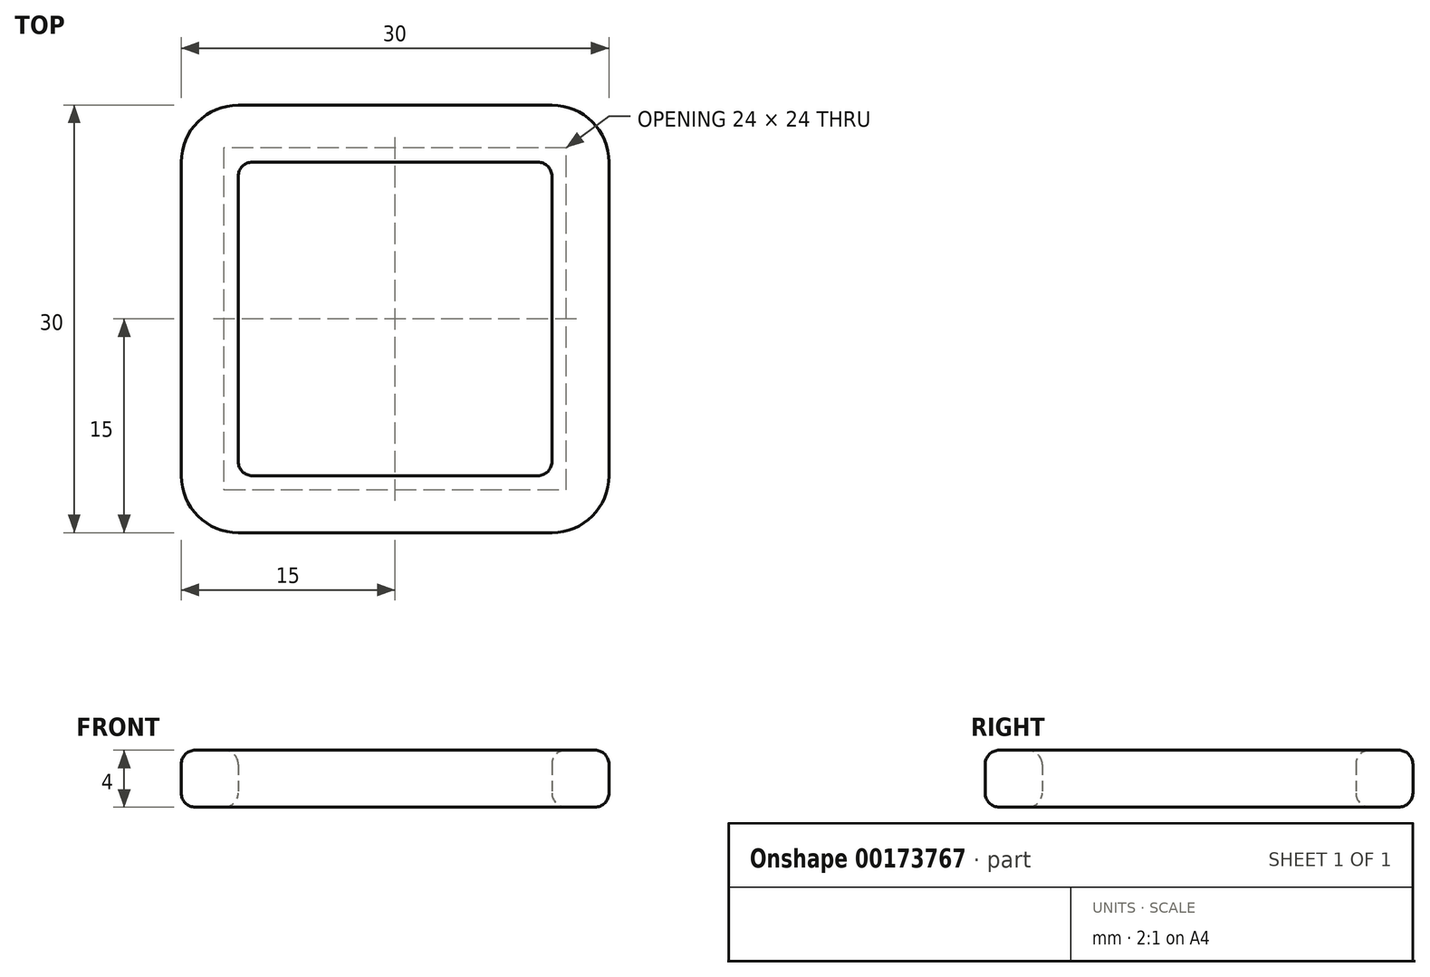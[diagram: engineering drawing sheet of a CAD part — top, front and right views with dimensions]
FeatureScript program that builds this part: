
annotation { "Feature Type Name" : "Feature", "Feature Type Description" : "" }
export const myFeature = defineFeature(function(context is Context, id is Id, definition is map)
    precondition{}
    {
        {
            var Q0;
            Q0=qCreatedBy(makeId("Top.planeOp"),FACE);
            var sketch = newSketch(context, id + "F0", { "sketchPlane" : qUnion([Q0])});
            skLineSegment(sketch, "E0.bottom", {"start": v(15, 15) * mm, "end": v(-15, 15) * mm});
            skLineSegment(sketch, "E0.top", {"start": v(15, -15) * mm, "end": v(-15, -15) * mm});
            skLineSegment(sketch, "E0.left", {"start": v(15, 15) * mm, "end": v(15, -15) * mm});
            skLineSegment(sketch, "E0.right", {"start": v(-15, 15) * mm, "end": v(-15, -15) * mm});
            skPoint(sketch, "E0.middle", {"position": v(0, 0) * mm});
            skSolve(sketch);
        }
        {
            var Q0;
            Q0=makeQuery(id+"F0.imprint","IMPRINT",FACE,{"disambiguationData":[TD([[makeQuery(id+"F0.imprint","IMPRINT",EDGE,{"derivedFrom":sQuery(id+"F0.wireOp",EDGE,"E0.bottom")}),1.0]])]});
            extrude(context, id + "F1", {"entities" : qUnion([Q0]), "depth" : 4 * mm});
        }
        {
            var Q0;
            Q0=makeQuery(id+"F1.opExtrude","CAP_FACE",FACE,{"disambiguationData":[OSD([sQuery(id+"F0.wireOp",EDGE,"E0.bottom"),sQuery(id+"F0.wireOp",EDGE,"E0.top"),sQuery(id+"F0.wireOp",EDGE,"E0.left"),sQuery(id+"F0.wireOp",EDGE,"E0.right")])],"isStart":false});
            var Q1;
            Q1=makeQuery(id+"F1.opExtrude","CAP_FACE",FACE,{"disambiguationData":[OSD([sQuery(id+"F0.wireOp",EDGE,"E0.bottom"),sQuery(id+"F0.wireOp",EDGE,"E0.top"),sQuery(id+"F0.wireOp",EDGE,"E0.left"),sQuery(id+"F0.wireOp",EDGE,"E0.right")])],"isStart":true});
            shell(context, id + "F2", {"entities" : qUnion([Q0, Q1]), "thickness" : 4 * mm});
        }
        {
            var Q0;
            Q0=makeQuery(id+"F2.opShell","OFFSET_EDGE",EDGE,{"disambiguationData":[OSD([sQuery(id+"F0.wireOp",EDGE,"E0.bottom"),sQuery(id+"F0.wireOp",EDGE,"E0.right")])]});
            var Q1;
            Q1=makeQuery(id+"F2.opShell","OFFSET_EDGE",EDGE,{"disambiguationData":[OSD([sQuery(id+"F0.wireOp",EDGE,"E0.bottom"),sQuery(id+"F0.wireOp",EDGE,"E0.left")])]});
            var Q2;
            Q2=makeQuery(id+"F2.opShell","OFFSET_EDGE",EDGE,{"disambiguationData":[OSD([sQuery(id+"F0.wireOp",EDGE,"E0.top"),sQuery(id+"F0.wireOp",EDGE,"E0.right")])]});
            var Q3;
            Q3=makeQuery(id+"F2.opShell","OFFSET_EDGE",EDGE,{"disambiguationData":[OSD([sQuery(id+"F0.wireOp",EDGE,"E0.top"),sQuery(id+"F0.wireOp",EDGE,"E0.left")])]});
            fillet(context, id + "F3", {"entities" : qUnion([Q0, Q1, Q2, Q3]), "radius" : 1 * mm, "tangentPropagation" : true, "allowEdgeOverflow" : false});
        }
        {
            var Q0;
            Q0=makeQuery(id+"F1.opExtrude","SWEPT_EDGE",EDGE,{"disambiguationData":[OSD([sQuery(id+"F0.wireOp",EDGE,"E0.bottom"),sQuery(id+"F0.wireOp",EDGE,"E0.right")])]});
            var Q1;
            Q1=makeQuery(id+"F1.opExtrude","SWEPT_EDGE",EDGE,{"disambiguationData":[OSD([sQuery(id+"F0.wireOp",EDGE,"E0.bottom"),sQuery(id+"F0.wireOp",EDGE,"E0.left")])]});
            var Q2;
            Q2=makeQuery(id+"F1.opExtrude","SWEPT_EDGE",EDGE,{"disambiguationData":[OSD([sQuery(id+"F0.wireOp",EDGE,"E0.top"),sQuery(id+"F0.wireOp",EDGE,"E0.right")])]});
            var Q3;
            Q3=makeQuery(id+"F1.opExtrude","SWEPT_EDGE",EDGE,{"disambiguationData":[OSD([sQuery(id+"F0.wireOp",EDGE,"E0.top"),sQuery(id+"F0.wireOp",EDGE,"E0.left")])]});
            fillet(context, id + "F4", {"entities" : qUnion([Q0, Q1, Q2, Q3]), "radius" : 4 * mm, "tangentPropagation" : true, "allowEdgeOverflow" : false});
        }
        {
            var Q0;
            {var subQ0=sQuery(id+"F0.wireOp",EDGE,"E0.left");Q0=makeQuery(id+"F2.opShell","OFFSET_EDGE",EDGE,{"disambiguationData":[OSD([subQ0]),TDD([makeQuery(id+"F1.opExtrude","CAP_EDGE",EDGE,{"disambiguationData":[OSD([subQ0])],"isStart":false})])]});}
            var Q1;
            Q1=makeQuery(id+"F1.opExtrude","CAP_EDGE",EDGE,{"disambiguationData":[OSD([sQuery(id+"F0.wireOp",EDGE,"E0.left")])],"isStart":false});
            var Q2;
            {var subQ0=sQuery(id+"F0.wireOp",EDGE,"E0.left");var subQ1=sQuery(id+"F0.wireOp",EDGE,"E0.bottom");Q2=makeQuery(id+"F4.opFillet","BLEND_EDGE",EDGE,{"blendedFrom":[makeQuery(id+"F1.opExtrude","SWEPT_EDGE",EDGE,{"disambiguationData":[OSD([subQ1,subQ0])]}),makeQuery(id+"F1.opExtrude","CAP_FACE",FACE,{"disambiguationData":[OSD([subQ1,sQuery(id+"F0.wireOp",EDGE,"E0.top"),subQ0,sQuery(id+"F0.wireOp",EDGE,"E0.right")])],"isStart":true})],"blendedInto":[makeQuery(id+"F1.opExtrude","CAP_FACE",FACE,{"disambiguationData":[OSD([subQ1,sQuery(id+"F0.wireOp",EDGE,"E0.top"),subQ0,sQuery(id+"F0.wireOp",EDGE,"E0.right")])],"isStart":true})]});}
            var Q3;
            {var subQ0=sQuery(id+"F0.wireOp",EDGE,"E0.left");var subQ1=sQuery(id+"F0.wireOp",EDGE,"E0.bottom");Q3=makeQuery(id+"F3.opFillet","BLEND_EDGE",EDGE,{"blendedFrom":[makeQuery(id+"F2.opShell","OFFSET_EDGE",EDGE,{"disambiguationData":[OSD([subQ1,subQ0])]}),makeQuery(id+"F1.opExtrude","CAP_FACE",FACE,{"disambiguationData":[OSD([subQ1,sQuery(id+"F0.wireOp",EDGE,"E0.top"),subQ0,sQuery(id+"F0.wireOp",EDGE,"E0.right")])],"isStart":true})],"blendedInto":[makeQuery(id+"F1.opExtrude","CAP_FACE",FACE,{"disambiguationData":[OSD([subQ1,sQuery(id+"F0.wireOp",EDGE,"E0.top"),subQ0,sQuery(id+"F0.wireOp",EDGE,"E0.right")])],"isStart":true})]});}
            fillet(context, id + "F5", {"entities" : qUnion([Q0, Q1, Q2, Q3]), "radius" : 1 * mm, "tangentPropagation" : true, "allowEdgeOverflow" : false});
        }
    });
